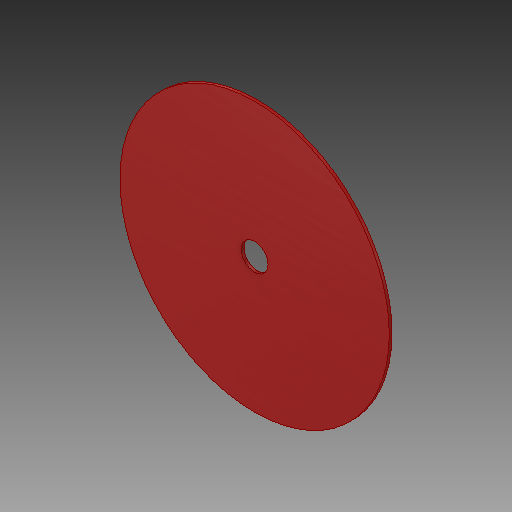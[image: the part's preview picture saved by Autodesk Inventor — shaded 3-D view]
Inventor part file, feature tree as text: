
AUTODESK INVENTOR PART (.ipt)
format: ipt  version: 2018 (Build 220112000, 112)  size: 99,840 bytes
history: native  units: mm
features: other x1, extrude x1, sketch x1
ambient origin geometry x8: Origin, YZ Plane, XZ Plane, XY Plane, X Axis, Y Axis, Z Axis, Center Point
bodies: Body1 (feature_tree)
feature tree (3):
  other  "Sega Circolare 300 mm"
  extrude  "Estrusione2"  Depth=300.0mm
  sketch  "Schizzo1"
